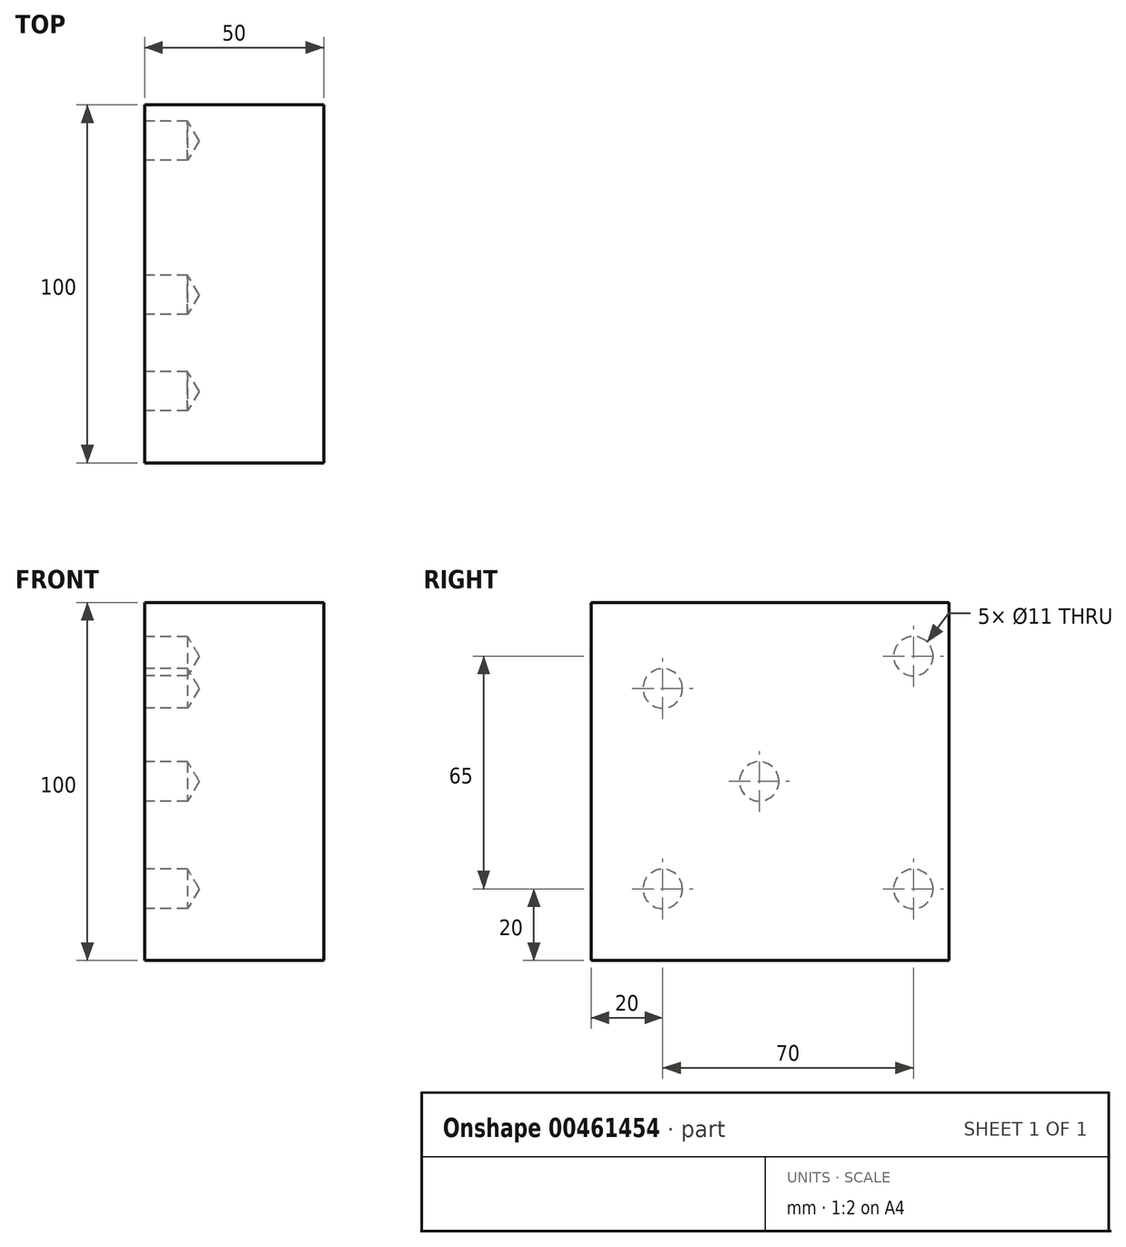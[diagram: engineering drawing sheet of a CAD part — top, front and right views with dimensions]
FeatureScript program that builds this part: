
annotation { "Feature Type Name" : "Feature", "Feature Type Description" : "" }
export const myFeature = defineFeature(function(context is Context, id is Id, definition is map)
    precondition{}
    {
        {
            var Q0;
            Q0=qCreatedBy(makeId("Top.planeOp"),FACE);
            var sketch = newSketch(context, id + "F0", { "sketchPlane" : qUnion([Q0])});
            skLineSegment(sketch, "E0", {"start": v(0, 65.3) * mm, "end": v(0, -52.73) * mm, "construction": true});
            skLineSegment(sketch, "E1", {"start": v(-44.52, 0) * mm, "end": v(56.48, 0) * mm, "construction": true});
            skLineSegment(sketch, "E2.bottom", {"start": v(-25, 50) * mm, "end": v(25, 50) * mm});
            skLineSegment(sketch, "E2.top", {"start": v(-25, -50) * mm, "end": v(25, -50) * mm});
            skLineSegment(sketch, "E2.left", {"start": v(-25, 50) * mm, "end": v(-25, -50) * mm});
            skLineSegment(sketch, "E2.right", {"start": v(25, 50) * mm, "end": v(25, -50) * mm});
            skSolve(sketch);
        }
        {
            var Q0;
            Q0=makeQuery(id+"F0.imprint","IMPRINT",FACE,{"disambiguationData":[TD([[makeQuery(id+"F0.imprint","IMPRINT",EDGE,{"derivedFrom":sQuery(id+"F0.wireOp",EDGE,"E2.bottom")}),-1.0]])]});
            extrude(context, id + "F1", {"entities" : qUnion([Q0]), "depth" : 50 * mm, "offsetDistance" : 25 * mm, "hasSecondDirection" : true, "secondDirectionOppositeDirection" : true, "secondDirectionDepth" : 50 * mm});
        }
        {
            var Q0;
            Q0=makeQuery(id+"F1.opExtrude","SWEPT_FACE",FACE,{"disambiguationData":[OSD([sQuery(id+"F0.wireOp",EDGE,"E2.left")])]});
            var sketch = newSketch(context, id + "F2", { "sketchPlane" : qUnion([Q0])});
            skPoint(sketch, "E3", {"position": v(3.05, 0) * mm});
            skPoint(sketch, "E4", {"position": v(30, 26) * mm});
            skPoint(sketch, "E5", {"position": v(-40, 35) * mm});
            skPoint(sketch, "E6", {"position": v(-40, -30) * mm});
            skPoint(sketch, "E7", {"position": v(30, -30) * mm});
            skSolve(sketch);
        }
        {
            var Q0;
            Q0=sQuery(id+"F2.wireOp",VERTEX,"E5");
            var Q1;
            Q1=sQuery(id+"F2.wireOp",VERTEX,"E4");
            var Q2;
            Q2=sQuery(id+"F2.wireOp",VERTEX,"E3");
            var Q3;
            Q3=sQuery(id+"F2.wireOp",VERTEX,"E7");
            var Q4;
            Q4=sQuery(id+"F2.wireOp",VERTEX,"E6");
            var Q5;
            Q5=makeQuery(id+"F1.opExtrude","SWEPT_BODY",BODY,{"disambiguationData":[OSD([sQuery(id+"F0.wireOp",EDGE,"E2.bottom"),sQuery(id+"F0.wireOp",EDGE,"E2.top"),sQuery(id+"F0.wireOp",EDGE,"E2.left"),sQuery(id+"F0.wireOp",EDGE,"E2.right")])]});
            hole(context, id + "F3", {"style" : HoleStyle.SIMPLE, "endStyle" : HoleEndStyle.BLIND, "standardTappedOrClearance" : lookupTablePath({ "standard" : "ISO", "fit" : "Normal", "size" : "M10", "type" : "Clearance" }), "standardBlindInLast" : lookupTablePath({ "fit" : "Standard", "standard" : "ISO", "size" : "M10", "type" : "Clearance" }), "holeDiameter" : 11 * mm, "majorDiameter" : 5 * mm, "holeDepth" : 12 * mm, "isTappedThrough" : true, "tappedDepth" : 12 * mm, "tapClearance" : 3, "locations" : qUnion([Q0, Q1, Q2, Q3, Q4]), "scope" : qUnion([Q5])});
        }
    });
